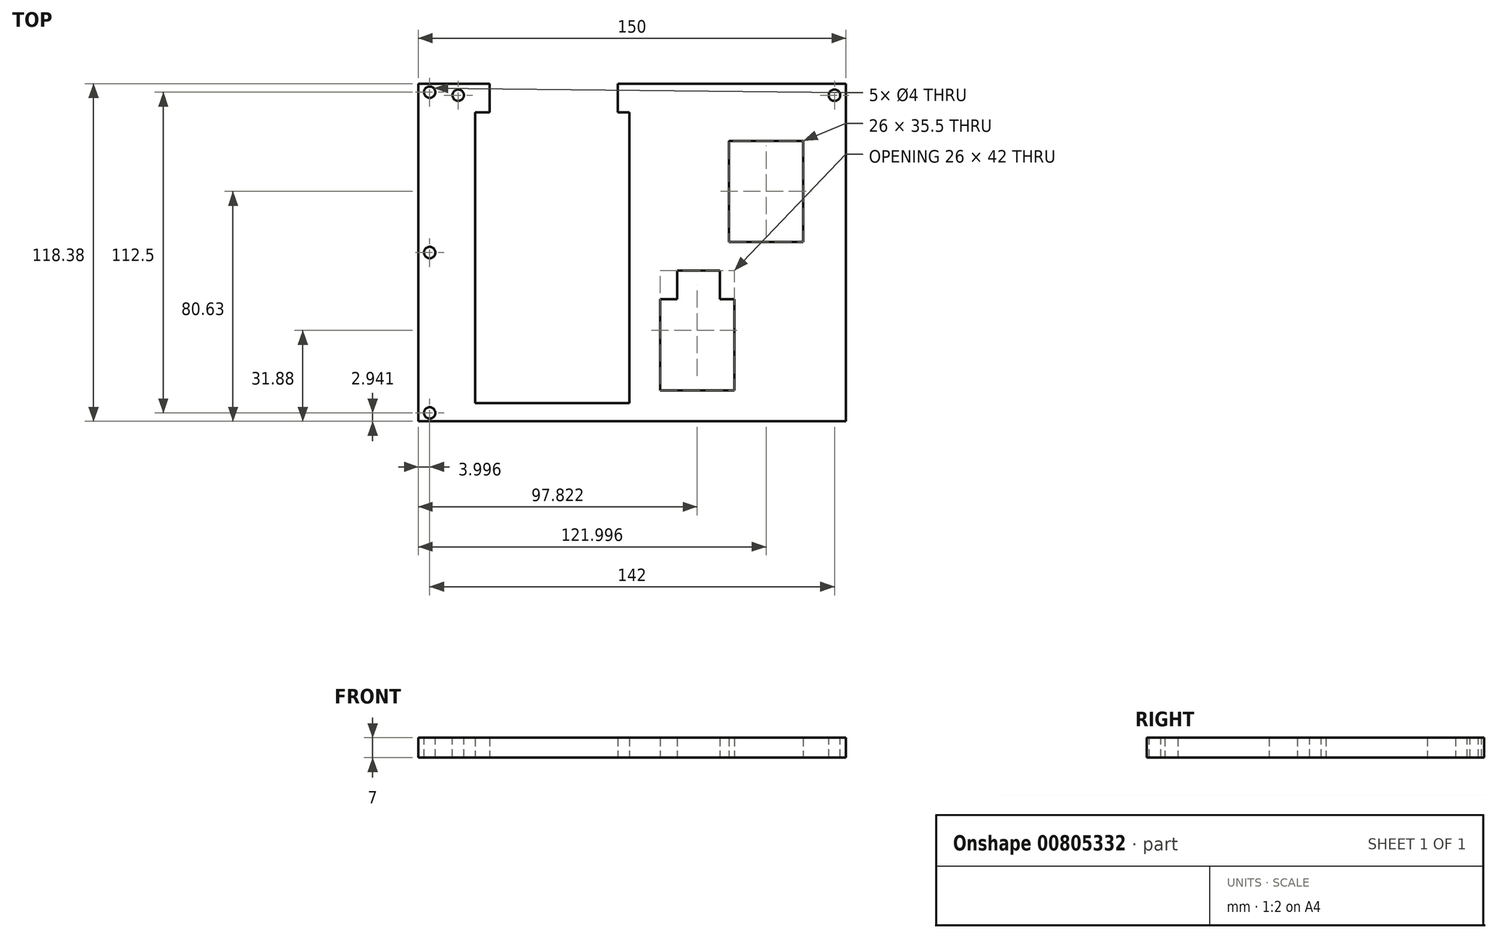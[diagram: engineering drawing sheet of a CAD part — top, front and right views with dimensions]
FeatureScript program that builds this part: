
annotation { "Feature Type Name" : "Feature", "Feature Type Description" : "" }
export const myFeature = defineFeature(function(context is Context, id is Id, definition is map)
    precondition{}
    {
        {
            var Q0;
            Q0=qCreatedBy(makeId("Top.planeOp"),FACE);
            var sketch = newSketch(context, id + "F0", { "sketchPlane" : qUnion([Q0])});
            skLineSegment(sketch, "E0.bottom", {"start": v(-61.61, 112) * mm, "end": v(78.39, 112) * mm});
            skLineSegment(sketch, "E0.top", {"start": v(-61.61, -113) * mm, "end": v(78.39, -113) * mm});
            skLineSegment(sketch, "E0.left", {"start": v(-61.61, 112) * mm, "end": v(-61.61, -113) * mm});
            skLineSegment(sketch, "E0.right", {"start": v(78.39, 112) * mm, "end": v(78.39, -113) * mm});
            skLineSegment(sketch, "E1.bottom", {"start": v(-51.61, 102) * mm, "end": v(2.39, 102) * mm});
            skLineSegment(sketch, "E1.top", {"start": v(-51.61, 0) * mm, "end": v(2.39, 0) * mm});
            skLineSegment(sketch, "E1.left", {"start": v(-51.61, 102) * mm, "end": v(-51.61, 0) * mm});
            skLineSegment(sketch, "E1.right", {"start": v(2.39, 102) * mm, "end": v(2.39, 0) * mm});
            skLineSegment(sketch, "E2.bottom", {"start": v(-52.61, -10) * mm, "end": v(68.39, -10) * mm});
            skLineSegment(sketch, "E2.top", {"start": v(-52.61, -91) * mm, "end": v(68.39, -91) * mm});
            skLineSegment(sketch, "E2.left", {"start": v(-52.61, -10) * mm, "end": v(-52.61, -91) * mm});
            skLineSegment(sketch, "E2.right", {"start": v(68.39, -10) * mm, "end": v(68.39, -91) * mm});
            skLineSegment(sketch, "E3.bottom", {"start": v(13.21, 36.5) * mm, "end": v(39.21, 36.5) * mm});
            skLineSegment(sketch, "E3.top", {"start": v(13.21, 4.5) * mm, "end": v(39.21, 4.5) * mm});
            skLineSegment(sketch, "E3.left", {"start": v(13.21, 36.5) * mm, "end": v(13.21, 4.5) * mm});
            skLineSegment(sketch, "E3.right", {"start": v(39.21, 36.5) * mm, "end": v(39.21, 4.5) * mm});
            skLineSegment(sketch, "E4.bottom", {"start": v(37.39, 92) * mm, "end": v(63.39, 92) * mm});
            skLineSegment(sketch, "E4.top", {"start": v(37.39, 56.5) * mm, "end": v(63.39, 56.5) * mm});
            skLineSegment(sketch, "E4.left", {"start": v(37.39, 92) * mm, "end": v(37.39, 56.5) * mm});
            skLineSegment(sketch, "E4.right", {"start": v(63.39, 92) * mm, "end": v(63.39, 56.5) * mm});
            skLineSegment(sketch, "E5", {"start": v(39.21, 36.5) * mm, "end": v(34.21, 36.5) * mm});
            skLineSegment(sketch, "E6", {"start": v(34.21, 36.5) * mm, "end": v(19.21, 36.5) * mm});
            skLineSegment(sketch, "E7", {"start": v(34.21, 36.5) * mm, "end": v(34.21, 46.5) * mm});
            skLineSegment(sketch, "E8.bottom", {"start": v(19.21, 36.5) * mm, "end": v(34.21, 36.5) * mm});
            skLineSegment(sketch, "E8.top", {"start": v(19.21, 46.5) * mm, "end": v(34.21, 46.5) * mm});
            skLineSegment(sketch, "E8.left", {"start": v(19.21, 36.5) * mm, "end": v(19.21, 46.5) * mm});
            skLineSegment(sketch, "E9.bottom", {"start": v(-46.61, 112) * mm, "end": v(-1.61, 112) * mm});
            skLineSegment(sketch, "E9.top", {"start": v(-46.61, 102) * mm, "end": v(-1.61, 102) * mm});
            skLineSegment(sketch, "E9.left", {"start": v(-46.61, 112) * mm, "end": v(-46.61, 102) * mm});
            skLineSegment(sketch, "E9.right", {"start": v(-1.61, 112) * mm, "end": v(-1.61, 102) * mm});
            skLineSegment(sketch, "E10", {"start": v(68.39, -10) * mm, "end": v(68.39, -30) * mm});
            skLineSegment(sketch, "E11.bottom", {"start": v(68.39, -30) * mm, "end": v(78.39, -30) * mm});
            skLineSegment(sketch, "E11.top", {"start": v(68.39, -10) * mm, "end": v(78.39, -10) * mm});
            skLineSegment(sketch, "E11.left", {"start": v(68.39, -30) * mm, "end": v(68.39, -10) * mm});
            skLineSegment(sketch, "E11.right", {"start": v(78.39, -30) * mm, "end": v(78.39, -10) * mm});
            skLineSegment(sketch, "E12.bottom", {"start": v(78.39, -7.6) * mm, "end": v(-61.61, -7.6) * mm});
            skLineSegment(sketch, "E12.top", {"start": v(78.39, -6.38) * mm, "end": v(-61.61, -6.38) * mm});
            skLineSegment(sketch, "E12.left", {"start": v(78.39, -7.6) * mm, "end": v(78.39, -6.38) * mm});
            skLineSegment(sketch, "E12.right", {"start": v(-61.61, -7.6) * mm, "end": v(-61.61, -6.38) * mm});
            skSolve(sketch);
        }
        {
            var Q0;
            Q0=makeQuery(id+"F0.imprint","IMPRINT",FACE,{"disambiguationData":[TD([[makeQuery(id+"F0.imprint","IMPRINT",EDGE,{"derivedFrom":sQuery(id+"F0.wireOp",EDGE,"E0.bottom")}),-1.0]])]});
            extrude(context, id + "F1", {"entities" : qUnion([Q0]), "depth" : 7 * mm, "offsetDistance" : 25.4 * mm});
        }
        {
            var Q0;
            Q0=makeQuery(id+"F1.opExtrude","SWEPT_FACE",FACE,{"disambiguationData":[OSD([sQuery(id+"F0.wireOp",EDGE,"E0.bottom")])]});
            var sketch = newSketch(context, id + "F2", { "sketchPlane" : qUnion([Q0])});
            skLineSegment(sketch, "E13.bottom", {"start": v(4.61, 0) * mm, "end": v(16.61, 0) * mm});
            skLineSegment(sketch, "E13.top", {"start": v(4.61, 5) * mm, "end": v(16.61, 5) * mm});
            skLineSegment(sketch, "E13.left", {"start": v(4.61, 0) * mm, "end": v(4.61, 5) * mm});
            skLineSegment(sketch, "E13.right", {"start": v(16.61, 0) * mm, "end": v(16.61, 5) * mm});
            skLineSegment(sketch, "E14.bottom", {"start": v(36.61, 0) * mm, "end": v(46.61, 0) * mm});
            skLineSegment(sketch, "E15.left", {"start": v(36.61, 0) * mm, "end": v(36.61, 0) * mm});
            skLineSegment(sketch, "E15.right", {"start": v(46.61, 0) * mm, "end": v(46.61, 0) * mm});
            skLineSegment(sketch, "E16.top", {"start": v(36.61, 10) * mm, "end": v(46.61, 10) * mm});
            skLineSegment(sketch, "E16.left", {"start": v(36.61, 0) * mm, "end": v(36.61, 10) * mm});
            skLineSegment(sketch, "E16.right", {"start": v(46.61, 0) * mm, "end": v(46.61, 10) * mm});
            skSolve(sketch);
        }
        {
            var Q0;
            Q0=makeQuery(id+"F1.opExtrude","CAP_FACE",FACE,{"disambiguationData":[OSD([sQuery(id+"F0.wireOp",EDGE,"E0.bottom"),sQuery(id+"F0.wireOp",EDGE,"E0.top"),sQuery(id+"F0.wireOp",EDGE,"E0.left"),sQuery(id+"F0.wireOp",EDGE,"E0.right"),sQuery(id+"F0.wireOp",EDGE,"E1.bottom"),sQuery(id+"F0.wireOp",EDGE,"E1.top"),sQuery(id+"F0.wireOp",EDGE,"E1.left"),sQuery(id+"F0.wireOp",EDGE,"E1.right"),sQuery(id+"F0.wireOp",EDGE,"E2.bottom"),sQuery(id+"F0.wireOp",EDGE,"E2.top"),sQuery(id+"F0.wireOp",EDGE,"E2.left"),sQuery(id+"F0.wireOp",EDGE,"E2.right"),sQuery(id+"F0.wireOp",EDGE,"E3.bottom"),sQuery(id+"F0.wireOp",EDGE,"E3.top"),sQuery(id+"F0.wireOp",EDGE,"E3.left"),sQuery(id+"F0.wireOp",EDGE,"E3.right"),sQuery(id+"F0.wireOp",EDGE,"E4.bottom"),sQuery(id+"F0.wireOp",EDGE,"E4.top"),sQuery(id+"F0.wireOp",EDGE,"E4.left"),sQuery(id+"F0.wireOp",EDGE,"E4.right")])],"isStart":false});
            var sketch = newSketch(context, id + "F3", { "sketchPlane" : qUnion([Q0])});
            skLineSegment(sketch, "E17", {"start": v(78.39, 112) * mm, "end": v(74.39, 112) * mm});
            skLineSegment(sketch, "E18", {"start": v(78.39, 112) * mm, "end": v(78.39, 116) * mm});
            skLineSegment(sketch, "E19.bottom", {"start": v(74.39, 112) * mm, "end": v(78.39, 112) * mm});
            skLineSegment(sketch, "E19.top", {"start": v(74.39, 116) * mm, "end": v(78.39, 116) * mm});
            skLineSegment(sketch, "E19.left", {"start": v(74.39, 112) * mm, "end": v(74.39, 116) * mm});
            skCircle(sketch, "E20", {"center": v(74.39, 116) * mm, "radius": 3.7 * mm});
            skLineSegment(sketch, "E21", {"start": v(-61.61, 112) * mm, "end": v(-61.61, 116) * mm});
            skLineSegment(sketch, "E22", {"start": v(-61.61, 116) * mm, "end": v(-61.61, 112) * mm});
            skLineSegment(sketch, "E23", {"start": v(-61.61, 112) * mm, "end": v(-61.61, 108) * mm});
            skLineSegment(sketch, "E24", {"start": v(-61.61, 108) * mm, "end": v(-61.61, 112) * mm});
            skLineSegment(sketch, "E25", {"start": v(-57.61, 112) * mm, "end": v(-61.61, 112) * mm});
            skLineSegment(sketch, "E26", {"start": v(78.39, 112) * mm, "end": v(78.39, 108) * mm});
            skLineSegment(sketch, "E27", {"start": v(78.39, 108) * mm, "end": v(78.39, 112) * mm});
            skLineSegment(sketch, "E28", {"start": v(-61.61, 112) * mm, "end": v(-57.61, 112) * mm});
            skLineSegment(sketch, "E29.bottom", {"start": v(-61.61, 116) * mm, "end": v(-57.61, 116) * mm});
            skLineSegment(sketch, "E29.right", {"start": v(-57.61, 116) * mm, "end": v(-57.61, 112) * mm});
            skLineSegment(sketch, "E30.top", {"start": v(-57.61, 108) * mm, "end": v(-61.61, 108) * mm});
            skLineSegment(sketch, "E30.left", {"start": v(-57.61, 112) * mm, "end": v(-57.61, 108) * mm});
            skLineSegment(sketch, "E31.top", {"start": v(74.39, 108) * mm, "end": v(78.39, 108) * mm});
            skLineSegment(sketch, "E31.left", {"start": v(74.39, 112) * mm, "end": v(74.39, 108) * mm});
            skCircle(sketch, "E32", {"center": v(74.39, 108) * mm, "radius": 4 * mm});
            skCircle(sketch, "E33", {"center": v(-57.61, 108) * mm, "radius": 4 * mm});
            skCircle(sketch, "E34", {"center": v(-57.61, 116) * mm, "radius": 4 * mm});
            skSolve(sketch);
        }
        {
            var Q0;
            Q0=sQuery(id+"F3.wireOp",VERTEX,"E31.top.start");
            var Q1;
            Q1=sQuery(id+"F3.wireOp",VERTEX,"E30.top.start");
            var Q2;
            Q2=sQuery(id+"F3.wireOp",VERTEX,"E29.bottom.end");
            var Q3;
            Q3=sQuery(id+"F3.wireOp",VERTEX,"E19.top.start");
            var Q4;
            Q4=makeQuery(id+"F1.opExtrude","SWEPT_BODY",BODY,{"disambiguationData":[OSD([sQuery(id+"F0.wireOp",EDGE,"E0.bottom"),sQuery(id+"F0.wireOp",EDGE,"E0.top"),sQuery(id+"F0.wireOp",EDGE,"E0.left"),sQuery(id+"F0.wireOp",EDGE,"E0.right"),sQuery(id+"F0.wireOp",EDGE,"E1.bottom"),sQuery(id+"F0.wireOp",EDGE,"E1.top"),sQuery(id+"F0.wireOp",EDGE,"E1.left"),sQuery(id+"F0.wireOp",EDGE,"E1.right"),sQuery(id+"F0.wireOp",EDGE,"E2.bottom"),sQuery(id+"F0.wireOp",EDGE,"E2.top"),sQuery(id+"F0.wireOp",EDGE,"E2.left"),sQuery(id+"F0.wireOp",EDGE,"E2.right"),sQuery(id+"F0.wireOp",EDGE,"E3.bottom"),sQuery(id+"F0.wireOp",EDGE,"E3.top"),sQuery(id+"F0.wireOp",EDGE,"E3.left"),sQuery(id+"F0.wireOp",EDGE,"E3.right"),sQuery(id+"F0.wireOp",EDGE,"E4.bottom"),sQuery(id+"F0.wireOp",EDGE,"E4.top"),sQuery(id+"F0.wireOp",EDGE,"E4.left"),sQuery(id+"F0.wireOp",EDGE,"E4.right")])]});
            hole(context, id + "F4", {"style" : HoleStyle.SIMPLE, "endStyle" : HoleEndStyle.THROUGH, "holeDiameter" : 4 * mm, "majorDiameter" : 6.35 * mm, "isTappedThrough" : true, "tappedDepth" : 12.7 * mm, "tapClearance" : 3, "locations" : qUnion([Q0, Q1, Q2, Q3]), "scope" : qUnion([Q4])});
        }
        {
            var Q0;
            Q0=makeQuery(id+"F1.opExtrude","SWEPT_FACE",FACE,{"disambiguationData":[OSD([sQuery(id+"F0.wireOp",EDGE,"E0.left")])]});
            extrude(context, id + "F5", {"entities" : qUnion([Q0]), "operationType" : NewBodyOperationType.ADD, "depth" : 10 * mm, "offsetDistance" : 25 * mm});
        }
        {
            var Q0;
            {var subQ0=sQuery(id+"F0.wireOp",EDGE,"E0.left");Q0=makeQuery(id+"F5.boolean.opBoolean","MERGE",FACE,{"derivedFrom":[makeQuery(id+"F1.opExtrude","CAP_FACE",FACE,{"disambiguationData":[OSD([sQuery(id+"F0.wireOp",EDGE,"E0.bottom"),sQuery(id+"F0.wireOp",EDGE,"E0.top"),subQ0,sQuery(id+"F0.wireOp",EDGE,"E0.right"),sQuery(id+"F0.wireOp",EDGE,"E1.bottom"),sQuery(id+"F0.wireOp",EDGE,"E1.top"),sQuery(id+"F0.wireOp",EDGE,"E1.left"),sQuery(id+"F0.wireOp",EDGE,"E1.right"),sQuery(id+"F0.wireOp",EDGE,"E2.bottom"),sQuery(id+"F0.wireOp",EDGE,"E2.top"),sQuery(id+"F0.wireOp",EDGE,"E2.left"),sQuery(id+"F0.wireOp",EDGE,"E2.right"),sQuery(id+"F0.wireOp",EDGE,"E3.bottom"),sQuery(id+"F0.wireOp",EDGE,"E3.top"),sQuery(id+"F0.wireOp",EDGE,"E3.left"),sQuery(id+"F0.wireOp",EDGE,"E3.right"),sQuery(id+"F0.wireOp",EDGE,"E4.bottom"),sQuery(id+"F0.wireOp",EDGE,"E4.top"),sQuery(id+"F0.wireOp",EDGE,"E4.left"),sQuery(id+"F0.wireOp",EDGE,"E4.right"),sQuery(id+"F0.wireOp",EDGE,"E5"),sQuery(id+"F0.wireOp",EDGE,"E8.top"),sQuery(id+"F0.wireOp",EDGE,"E8.left"),sQuery(id+"F0.wireOp",EDGE,"E7"),sQuery(id+"F0.wireOp",EDGE,"E9.left"),sQuery(id+"F0.wireOp",EDGE,"E9.right")])],"isStart":false}),makeQuery(id+"F5.opExtrude","SWEPT_FACE",FACE,{"disambiguationData":[OSD([subQ0]),TDD([makeQuery(id+"F1.opExtrude","CAP_EDGE",EDGE,{"disambiguationData":[OSD([subQ0])],"isStart":false})])]})]});}
            var sketch = newSketch(context, id + "F6", { "sketchPlane" : qUnion([Q0])});
            skLineSegment(sketch, "E35", {"start": v(-71.61, 52.81) * mm, "end": v(-71.61, 109.06) * mm});
            skLineSegment(sketch, "E36", {"start": v(-71.61, 52.81) * mm, "end": v(-71.61, -3.44) * mm});
            skLineSegment(sketch, "E37", {"start": v(-71.61, -3.44) * mm, "end": v(-67.61, -3.44) * mm});
            skLineSegment(sketch, "E38", {"start": v(-71.61, 52.81) * mm, "end": v(-67.61, 52.81) * mm});
            skLineSegment(sketch, "E39", {"start": v(-71.61, 109.06) * mm, "end": v(-67.61, 109.06) * mm});
            skCircle(sketch, "E40", {"center": v(-67.61, 109.06) * mm, "radius": 2 * mm});
            skSolve(sketch);
        }
        {
            var Q0;
            Q0=sQuery(id+"F6.wireOp",VERTEX,"E39.end");
            var Q1;
            Q1=sQuery(id+"F6.wireOp",VERTEX,"E38.end");
            var Q2;
            Q2=sQuery(id+"F6.wireOp",VERTEX,"E37.end");
            var Q3;
            Q3=makeQuery(id+"F1.opExtrude","SWEPT_BODY",BODY,{"disambiguationData":[OSD([sQuery(id+"F0.wireOp",EDGE,"E0.bottom"),sQuery(id+"F0.wireOp",EDGE,"E0.top"),sQuery(id+"F0.wireOp",EDGE,"E0.left"),sQuery(id+"F0.wireOp",EDGE,"E0.right"),sQuery(id+"F0.wireOp",EDGE,"E1.bottom"),sQuery(id+"F0.wireOp",EDGE,"E1.top"),sQuery(id+"F0.wireOp",EDGE,"E1.left"),sQuery(id+"F0.wireOp",EDGE,"E1.right"),sQuery(id+"F0.wireOp",EDGE,"E2.bottom"),sQuery(id+"F0.wireOp",EDGE,"E2.top"),sQuery(id+"F0.wireOp",EDGE,"E2.left"),sQuery(id+"F0.wireOp",EDGE,"E2.right"),sQuery(id+"F0.wireOp",EDGE,"E3.bottom"),sQuery(id+"F0.wireOp",EDGE,"E3.top"),sQuery(id+"F0.wireOp",EDGE,"E3.left"),sQuery(id+"F0.wireOp",EDGE,"E3.right"),sQuery(id+"F0.wireOp",EDGE,"E4.bottom"),sQuery(id+"F0.wireOp",EDGE,"E4.top"),sQuery(id+"F0.wireOp",EDGE,"E4.left"),sQuery(id+"F0.wireOp",EDGE,"E4.right"),sQuery(id+"F0.wireOp",EDGE,"E5"),sQuery(id+"F0.wireOp",EDGE,"E8.top"),sQuery(id+"F0.wireOp",EDGE,"E8.left"),sQuery(id+"F0.wireOp",EDGE,"E7"),sQuery(id+"F0.wireOp",EDGE,"E9.left"),sQuery(id+"F0.wireOp",EDGE,"E9.right")])]});
            hole(context, id + "F7", {"style" : HoleStyle.SIMPLE, "endStyle" : HoleEndStyle.THROUGH, "holeDiameter" : 4 * mm, "majorDiameter" : 5 * mm, "isTappedThrough" : true, "tappedDepth" : 12 * mm, "tapClearance" : 3, "locations" : qUnion([Q0, Q1, Q2]), "scope" : qUnion([Q3])});
        }
    });
